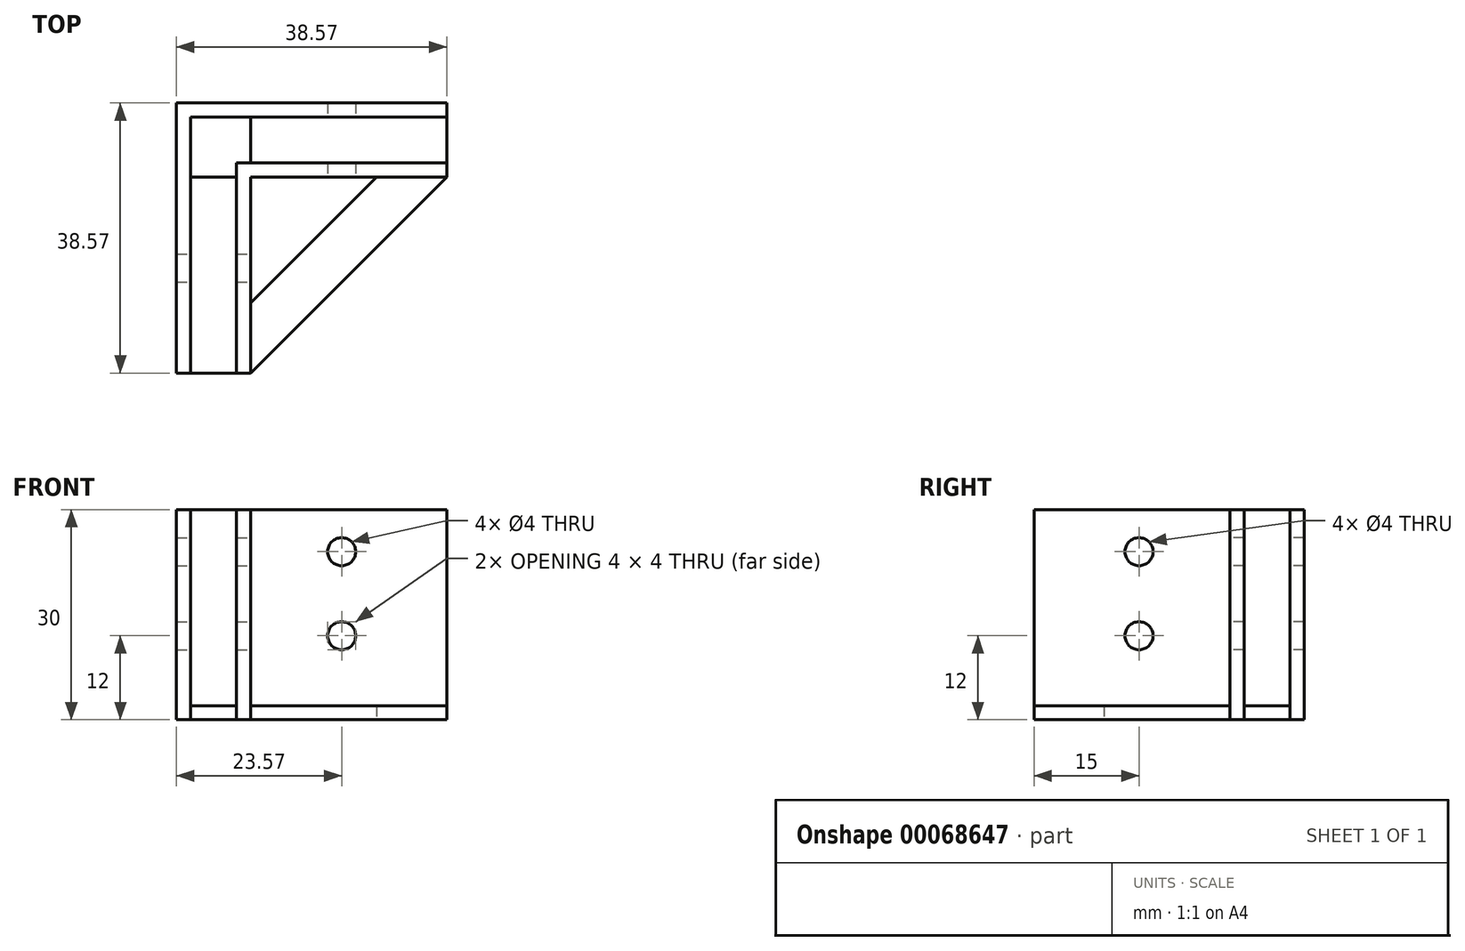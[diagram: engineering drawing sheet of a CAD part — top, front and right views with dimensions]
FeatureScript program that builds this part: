
annotation { "Feature Type Name" : "Feature", "Feature Type Description" : "" }
export const myFeature = defineFeature(function(context is Context, id is Id, definition is map)
    precondition{}
    {
        {
            var Q0;
            Q0=qCreatedBy(makeId("Top.planeOp"),FACE);
            var sketch = newSketch(context, id + "F0", { "sketchPlane" : qUnion([Q0])});
            skLineSegment(sketch, "E0", {"start": v(30, 0) * mm, "end": v(30, 6.57) * mm});
            skLineSegment(sketch, "E1", {"start": v(0, 0) * mm, "end": v(30, 0) * mm});
            skLineSegment(sketch, "E2", {"start": v(0, 0) * mm, "end": v(0, -30) * mm});
            skLineSegment(sketch, "E3", {"start": v(0, -30) * mm, "end": v(-6.57, -30) * mm});
            skLineSegment(sketch, "E4", {"start": v(-6.57, -30) * mm, "end": v(-6.57, 6.57) * mm});
            skLineSegment(sketch, "E5", {"start": v(-6.57, 6.57) * mm, "end": v(30, 6.57) * mm});
            skLineSegment(sketch, "E6", {"start": v(30, 6.57) * mm, "end": v(30, 8.57) * mm});
            skLineSegment(sketch, "E7", {"start": v(-6.57, -30) * mm, "end": v(-8.57, -30) * mm});
            skLineSegment(sketch, "E8", {"start": v(-6.57, 6.57) * mm, "end": v(-6.57, 8.57) * mm});
            skLineSegment(sketch, "E9", {"start": v(-6.57, 6.57) * mm, "end": v(-8.57, 6.57) * mm});
            skLineSegment(sketch, "E10", {"start": v(-8.57, -30) * mm, "end": v(-8.57, 6.57) * mm});
            skLineSegment(sketch, "E11", {"start": v(30, 8.57) * mm, "end": v(-6.57, 8.57) * mm});
            skLineSegment(sketch, "E12.bottom", {"start": v(-6.57, 8.57) * mm, "end": v(-8.57, 8.57) * mm});
            skLineSegment(sketch, "E12.left", {"start": v(-6.57, 8.57) * mm, "end": v(-6.57, 6.57) * mm});
            skLineSegment(sketch, "E12.right", {"start": v(-8.57, 8.57) * mm, "end": v(-8.57, 6.57) * mm});
            skLineSegment(sketch, "E13.bottom", {"start": v(0, 0) * mm, "end": v(2, 0) * mm});
            skLineSegment(sketch, "E13.top", {"start": v(0, -2) * mm, "end": v(2, -2) * mm});
            skLineSegment(sketch, "E13.left", {"start": v(0, 0) * mm, "end": v(0, -2) * mm});
            skLineSegment(sketch, "E13.right", {"start": v(2, 0) * mm, "end": v(2, -2) * mm});
            skLineSegment(sketch, "E14", {"start": v(0, -30) * mm, "end": v(2, -30) * mm});
            skLineSegment(sketch, "E15", {"start": v(30, 0) * mm, "end": v(30, -2) * mm});
            skLineSegment(sketch, "E16", {"start": v(30, -2) * mm, "end": v(2, -2) * mm});
            skLineSegment(sketch, "E17", {"start": v(2, -30) * mm, "end": v(2, -2) * mm});
            skLineSegment(sketch, "E18", {"start": v(2, 0) * mm, "end": v(2, 6.57) * mm});
            skLineSegment(sketch, "E19", {"start": v(0, -2) * mm, "end": v(-6.57, -2) * mm});
            skSolve(sketch);
        }
        {
            var Q0;
            Q0=makeQuery(id+"F0.imprint","IMPRINT",FACE,{"disambiguationData":[TD([[makeQuery(id+"F0.imprint","IMPRINT",EDGE,{"derivedFrom":sQuery(id+"F0.wireOp",EDGE,"E4")}),1.0]])]});
            var Q1;
            Q1=makeQuery(id+"F0.imprint","IMPRINT",FACE,{"disambiguationData":[TD([[makeQuery(id+"F0.imprint","IMPRINT",EDGE,{"derivedFrom":sQuery(id+"F0.wireOp",EDGE,"E12.bottom")}),1.0]])]});
            var Q2;
            Q2=makeQuery(id+"F0.imprint","IMPRINT",FACE,{"disambiguationData":[TD([[makeQuery(id+"F0.imprint","IMPRINT",EDGE,{"derivedFrom":sQuery(id+"F0.wireOp",EDGE,"E5")}),1.0]])]});
            var Q3;
            Q3=makeQuery(id+"F0.imprint","IMPRINT",FACE,{"disambiguationData":[TD([[makeQuery(id+"F0.imprint","IMPRINT",EDGE,{"derivedFrom":sQuery(id+"F0.wireOp",EDGE,"E1")}),-1.0]])]});
            var Q4;
            Q4=makeQuery(id+"F0.imprint","IMPRINT",FACE,{"disambiguationData":[TD([[makeQuery(id+"F0.imprint","IMPRINT",EDGE,{"derivedFrom":sQuery(id+"F0.wireOp",EDGE,"E2")}),1.0]])]});
            var Q5;
            Q5=makeQuery(id+"F0.imprint","IMPRINT",FACE,{"disambiguationData":[TD([[makeQuery(id+"F0.imprint","IMPRINT",EDGE,{"derivedFrom":sQuery(id+"F0.wireOp",EDGE,"E13.bottom")}),-1.0]])]});
            var Q6;
            {var subQ4=sQuery(id+"F0.wireOp",EDGE,"3CWI9ahr-eMba-zCJy-X0Qq-DMD4ySDIpEOK");Q6=makeQuery(id+"F0.imprint","IMPRINT",FACE,{"disambiguationData":[TD([[makeQuery(id+"F0.imprint","IMPRINT",EDGE,{"derivedFrom":subQ4}),1.0]])]});}
            var Q7;
            Q7=makeQuery(id+"F0.imprint","IMPRINT",FACE,{"disambiguationData":[TD([[makeQuery(id+"F0.imprint","IMPRINT",EDGE,{"derivedFrom":sQuery(id+"F0.wireOp",EDGE,"E13.bottom")}),1.0]])]});
            extrude(context, id + "F1", {"entities" : qUnion([Q0, Q1, Q2, Q3, Q4, Q5, Q6, Q7]), "depth" : 30 * mm});
        }
        {
            var Q0;
            Q0=makeQuery(id+"F0.imprint","IMPRINT",FACE,{"disambiguationData":[TD([[makeQuery(id+"F0.imprint","IMPRINT",EDGE,{"derivedFrom":sQuery(id+"F0.wireOp",EDGE,"E0")}),1.0]])]});
            var Q1;
            Q1=makeQuery(id+"F0.imprint","IMPRINT",FACE,{"disambiguationData":[TD([[makeQuery(id+"F0.imprint","IMPRINT",EDGE,{"derivedFrom":sQuery(id+"F0.wireOp",EDGE,"E2")}),-1.0]])]});
            extrude(context, id + "F2", {"entities" : qUnion([Q0, Q1]), "depth" : 2 * mm});
        }
        {
            var Q0;
            Q0=makeQuery(id+"F2.opExtrude","CAP_FACE",FACE,{"disambiguationData":[OSD([sQuery(id+"F0.wireOp",EDGE,"E0"),sQuery(id+"F0.wireOp",EDGE,"E1"),sQuery(id+"F0.wireOp",EDGE,"E2"),sQuery(id+"F0.wireOp",EDGE,"E3"),sQuery(id+"F0.wireOp",EDGE,"E4"),sQuery(id+"F0.wireOp",EDGE,"E5"),sQuery(id+"F0.wireOp",EDGE,"E13.bottom"),sQuery(id+"F0.wireOp",EDGE,"E13.left")])],"isStart":true});
            var sketch = newSketch(context, id + "F3", { "sketchPlane" : qUnion([Q0])});
            skLineSegment(sketch, "E20.0", {"start": v(30, 2) * mm, "end": v(2, 2) * mm});
            skLineSegment(sketch, "E21.0", {"start": v(2, 30) * mm, "end": v(2, 2) * mm});
            skLineSegment(sketch, "E22", {"start": v(2, 30) * mm, "end": v(30, 2) * mm});
            skLineSegment(sketch, "E23", {"start": v(2, 30) * mm, "end": v(2, 20) * mm});
            skLineSegment(sketch, "E24", {"start": v(30, 2) * mm, "end": v(20, 2) * mm});
            skLineSegment(sketch, "E25", {"start": v(2, 20) * mm, "end": v(20, 2) * mm});
            skSolve(sketch);
        }
        {
            var Q0;
            Q0=makeQuery(id+"F3.imprint","IMPRINT",FACE,{"disambiguationData":[TD([[makeQuery(id+"F3.imprint","IMPRINT",EDGE,{"derivedFrom":sQuery(id+"F3.wireOp",EDGE,"E22")}),-1.0]])]});
            extrude(context, id + "F4", {"entities" : qUnion([Q0]), "oppositeDirection" : true, "depth" : 2 * mm});
        }
        {
            var Q0;
            Q0=makeQuery(id+"F1.opExtrude","SWEPT_FACE",FACE,{"disambiguationData":[OSD([sQuery(id+"F0.wireOp",EDGE,"E17")])]});
            var sketch = newSketch(context, id + "F5", { "sketchPlane" : qUnion([Q0])});
            skLineSegment(sketch, "E26.0", {"start": v(-30, 2) * mm, "end": v(-2, 2) * mm});
            skLineSegment(sketch, "E27.0", {"start": v(-30, 30) * mm, "end": v(-30, 0) * mm});
            skLineSegment(sketch, "E28", {"start": v(-15, 2) * mm, "end": v(-15, 12) * mm});
            skLineSegment(sketch, "E29", {"start": v(-15, 12) * mm, "end": v(-15, 24) * mm});
            skCircle(sketch, "E30", {"center": v(-15, 24) * mm, "radius": 2 * mm});
            skCircle(sketch, "E31", {"center": v(-15, 12) * mm, "radius": 2 * mm});
            skSolve(sketch);
        }
        {
            var Q0;
            Q0=makeQuery(id+"F5.imprint","IMPRINT",FACE,{"disambiguationData":[TD([[makeQuery(id+"F5.imprint","IMPRINT",EDGE,{"derivedFrom":sQuery(id+"F5.wireOp",EDGE,"E30")}),1.0]])]});
            var Q1;
            {var subQ0=sQuery(id+"F5.wireOp",EDGE,"E29");var subQ1=sQuery(id+"F5.wireOp",EDGE,"E28");var subQ2=makeQuery(id+"F5.imprint","INTERSECT",VERTEX,{"derivedFrom":[subQ1,subQ0]});Q1=makeQuery(id+"F5.imprint","IMPRINT",FACE,{"disambiguationData":[TD([[makeQuery(id+"F5.imprint","IMPRINT",EDGE,{"disambiguationData":[TD([[subQ2,1.0]])],"derivedFrom":subQ1}),-1.0]])]});}
            var Q2;
            {var subQ0=sQuery(id+"F5.wireOp",EDGE,"E29");var subQ1=sQuery(id+"F5.wireOp",EDGE,"E28");var subQ2=makeQuery(id+"F5.imprint","INTERSECT",VERTEX,{"derivedFrom":[subQ1,subQ0]});Q2=makeQuery(id+"F5.imprint","IMPRINT",FACE,{"disambiguationData":[TD([[makeQuery(id+"F5.imprint","IMPRINT",EDGE,{"disambiguationData":[TD([[subQ2,1.0]])],"derivedFrom":subQ1}),1.0]])]});}
            extrude(context, id + "F6", {"entities" : qUnion([Q0, Q1, Q2]), "oppositeDirection" : true, "depth" : 20 * mm});
        }
        {
            var Q0;
            Q0=makeQuery(id+"F1.opExtrude","SWEPT_FACE",FACE,{"disambiguationData":[OSD([sQuery(id+"F0.wireOp",EDGE,"E16")])]});
            var sketch = newSketch(context, id + "F7", { "sketchPlane" : qUnion([Q0])});
            skLineSegment(sketch, "E32.0", {"start": v(2, 2) * mm, "end": v(30, 2) * mm});
            skLineSegment(sketch, "E33", {"start": v(30, 2) * mm, "end": v(15, 2) * mm});
            skLineSegment(sketch, "E34", {"start": v(15, 2) * mm, "end": v(15, 12) * mm});
            skLineSegment(sketch, "E35", {"start": v(15, 12) * mm, "end": v(15, 24) * mm});
            skCircle(sketch, "E36", {"center": v(15, 24) * mm, "radius": 2 * mm});
            skCircle(sketch, "E37", {"center": v(15, 12) * mm, "radius": 2 * mm});
            skSolve(sketch);
        }
        {
            var Q0;
            Q0=makeQuery(id+"F7.imprint","IMPRINT",FACE,{"disambiguationData":[TD([[makeQuery(id+"F7.imprint","IMPRINT",EDGE,{"derivedFrom":sQuery(id+"F7.wireOp",EDGE,"E36")}),1.0]])]});
            var Q1;
            {var subQ0=sQuery(id+"F7.wireOp",EDGE,"E35");var subQ1=sQuery(id+"F7.wireOp",EDGE,"E34");var subQ2=makeQuery(id+"F7.imprint","INTERSECT",VERTEX,{"derivedFrom":[subQ1,subQ0]});Q1=makeQuery(id+"F7.imprint","IMPRINT",FACE,{"disambiguationData":[TD([[makeQuery(id+"F7.imprint","IMPRINT",EDGE,{"disambiguationData":[TD([[subQ2,1.0]])],"derivedFrom":subQ1}),1.0]])]});}
            var Q2;
            {var subQ0=sQuery(id+"F7.wireOp",EDGE,"E35");var subQ1=sQuery(id+"F7.wireOp",EDGE,"E34");var subQ2=makeQuery(id+"F7.imprint","INTERSECT",VERTEX,{"derivedFrom":[subQ1,subQ0]});Q2=makeQuery(id+"F7.imprint","IMPRINT",FACE,{"disambiguationData":[TD([[makeQuery(id+"F7.imprint","IMPRINT",EDGE,{"disambiguationData":[TD([[subQ2,1.0]])],"derivedFrom":subQ1}),-1.0]])]});}
            extrude(context, id + "F8", {"entities" : qUnion([Q0, Q1, Q2]), "oppositeDirection" : true, "depth" : 25 * mm});
        }
        {
            var Q0;
            Q0=makeQuery(id+"F8.opExtrude","SWEPT_BODY",BODY,{"disambiguationData":[OSD([sQuery(id+"F7.wireOp",EDGE,"E36")])]});
            var Q1;
            Q1=makeQuery(id+"F6.opExtrude","SWEPT_BODY",BODY,{"disambiguationData":[OSD([sQuery(id+"F5.wireOp",EDGE,"E30")])]});
            var Q2;
            Q2=makeQuery(id+"F6.opExtrude","SWEPT_BODY",BODY,{"disambiguationData":[OSD([sQuery(id+"F5.wireOp",EDGE,"E31")])]});
            var Q3;
            Q3=makeQuery(id+"F8.opExtrude","SWEPT_BODY",BODY,{"disambiguationData":[OSD([sQuery(id+"F7.wireOp",EDGE,"E37")])]});
            var Q4;
            Q4=makeQuery(id+"F1.opExtrude","SWEPT_BODY",BODY,{"disambiguationData":[OSD([sQuery(id+"F0.wireOp",EDGE,"E4"),sQuery(id+"F0.wireOp",EDGE,"E5"),sQuery(id+"F0.wireOp",EDGE,"E6"),sQuery(id+"F0.wireOp",EDGE,"E7"),sQuery(id+"F0.wireOp",EDGE,"E10"),sQuery(id+"F0.wireOp",EDGE,"E11"),sQuery(id+"F0.wireOp",EDGE,"E12.bottom"),sQuery(id+"F0.wireOp",EDGE,"E12.right")])]});
            var Q5;
            Q5=makeQuery(id+"F1.opExtrude","SWEPT_BODY",BODY,{"disambiguationData":[OSD([sQuery(id+"F0.wireOp",EDGE,"E1"),sQuery(id+"F0.wireOp",EDGE,"E2"),sQuery(id+"F0.wireOp",EDGE,"E13.bottom"),sQuery(id+"F0.wireOp",EDGE,"E13.left"),sQuery(id+"F0.wireOp",EDGE,"E14"),sQuery(id+"F0.wireOp",EDGE,"E15"),sQuery(id+"F0.wireOp",EDGE,"E16"),sQuery(id+"F0.wireOp",EDGE,"E17")])]});
            booleanBodies(context, id + "F9", {"operationType" : BooleanOperationType.SUBTRACTION, "tools" : qUnion([Q0, Q1, Q2, Q3]), "targets" : qUnion([Q4, Q5])});
        }
    });
